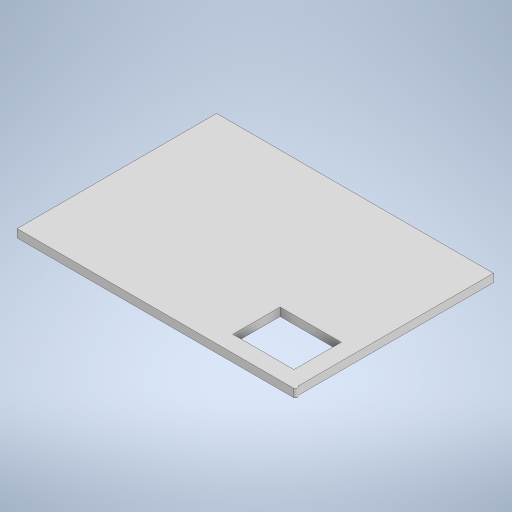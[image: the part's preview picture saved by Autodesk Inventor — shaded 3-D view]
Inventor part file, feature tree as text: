
AUTODESK INVENTOR PART (.ipt)
format: ipt  version: 2023 (Build 270158000, 158)  size: 545,280 bytes
history: native  units: in
note: dims shown in document units (in); Inventor stores cm internally (conversion verified against a paired STEP export)
features: extrude x3, sketch x3
ambient origin geometry x8: Origin, YZ Plane, XZ Plane, XY Plane, X Axis, Y Axis, Z Axis, Center Point
bodies: Solid1 (feature_tree)
feature tree (6):
  extrude  "Extrusion1"  Depth=2.6772in
  extrude  "Extrusion2"  Depth=0.0787in
  extrude  "Extrusion3"  Depth=0.0787in TaperAngle=0.0deg
  sketch  "Sketch1"  dims[d0=1.9291in d1=2.6772in]
  sketch  "Sketch3"  dims[d2=0.0787in d3=0.0in d6=0.0394in]
  sketch  "Sketch4"  dims[d9=0.962in d10=0.0787in d11=0.0in d12=0.5906in d13=0.4567in d14=0.1575in d15=0.1575in d16=0.3937in d17=0.0in]
